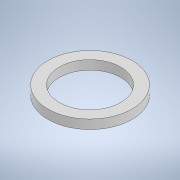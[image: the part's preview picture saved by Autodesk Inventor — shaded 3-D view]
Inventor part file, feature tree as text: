
AUTODESK INVENTOR PART (.ipt)
format: ipt  version: 2022 (Build 260153000, 153)  size: 101,376 bytes
history: native  units: mm
features: extrude x1, sketch x1
ambient origin geometry x8: Origin, YZ Plane, XZ Plane, XY Plane, X Axis, Y Axis, Z Axis, Center Point
bodies: Solid1 (feature_tree)
feature tree (2):
  extrude  "Extrusion1"  Depth=2.7mm
  sketch  "Sketch1"  dims[d0=18.3mm d1=25.0mm d2=2.7mm d3=0.0mm]
